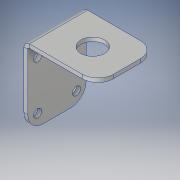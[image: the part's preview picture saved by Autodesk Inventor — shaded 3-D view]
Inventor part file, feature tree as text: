
AUTODESK INVENTOR PART (.ipt)
format: ipt  version: 2019 (Build 230136000, 136)  size: 195,072 bytes
history: native  units: mm
features: other x4, sheet_metal_op x3, sketch x3, chamfer x1
ambient origin geometry x8: Origin, YZ Plane, XZ Plane, XY Plane, X Axis, Y Axis, Z Axis, Center Point
bodies: Body1 (feature_tree)
feature tree (11):
  sheet_metal_op  "Contour Flange2"
  chamfer  "Corner Round1"
  sketch  "Sketch1"  dims[d0=40.0mm]
  other  "Plate2"
  sheet_metal_op  "Bend2"
  sheet_metal_op  "Corner2"
  sketch  "Sketch2"  dims[d1=38.0mm]
  sketch  "Sketch3"  dims[d13=2.0mm d14=0.2mm d15=0.2mm d16=0.2mm d17=0.8mm d18=30.0mm d19=0.8mm d20=2.0mm d21=8.0mm d22=0.2mm d23=0.8mm d24=12.2mm d25=2.0mm d26=0.0mm d27=20.0mm d28=25.0mm d29=4.2mm d30=2.0mm d31=0.0mm d32=8.0mm]
  other  "Cut1"
  other  "Cut2"
  other  "Definition1"
